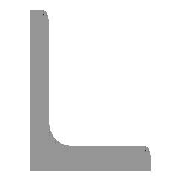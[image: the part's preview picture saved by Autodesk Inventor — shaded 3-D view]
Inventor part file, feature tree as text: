
AUTODESK INVENTOR PART (.ipt)
format: ipt  version: 2013 (Build 170138000, 138)  size: 150,528 bytes
history: native  units: mm (DEFAULTED — no unit token found)
features: plane x7, other x4, sketch x4, extrude x2
ambient origin geometry x8: Origin, YZ Plane, XZ Plane, XY Plane, X Axis, Y Axis, Z Axis, Center Point
bodies: Solid1 (feature_tree), Body (feature_tree)
feature tree (17):
  parser-record x1  (decoder bookkeeping rows leaked as tree rows — omitted from the tree; the rows remain in map.json)
  other  "Driven Length"
  other  "Start plane"
  other  "End plane"
  plane  "Work Plane4"
  plane  "Work Plane5"
  plane  "Work Plane6"
  extrude  "Extrusion2"  Depth=38.1mm
  plane  "Work Plane7"
  plane  "Work Plane8"
  plane  "Work Plane9"
  extrude  "Extrusion3"  Depth=4.7625mm
  sketch  "Sketch3"  dims[d0=38.1mm d1=38.1mm]
  plane  "Work Plane3"
  sketch  "Sketch4"  dims[d2=4.7625mm d3=4.7625mm]
  sketch  "Sketch5"  dims[d4=558.8mm]
  sketch  "Sketch6"  dims[d5=0.0mm d10=0.0mm d11=0.0mm d12=-0.0mm d13=558.8mm d14=4.826mm d15=2.286mm d16=90.0deg d17=558.8mm d18=3.302mm d19=0.0mm d20=3.302mm d21=0.0mm]
